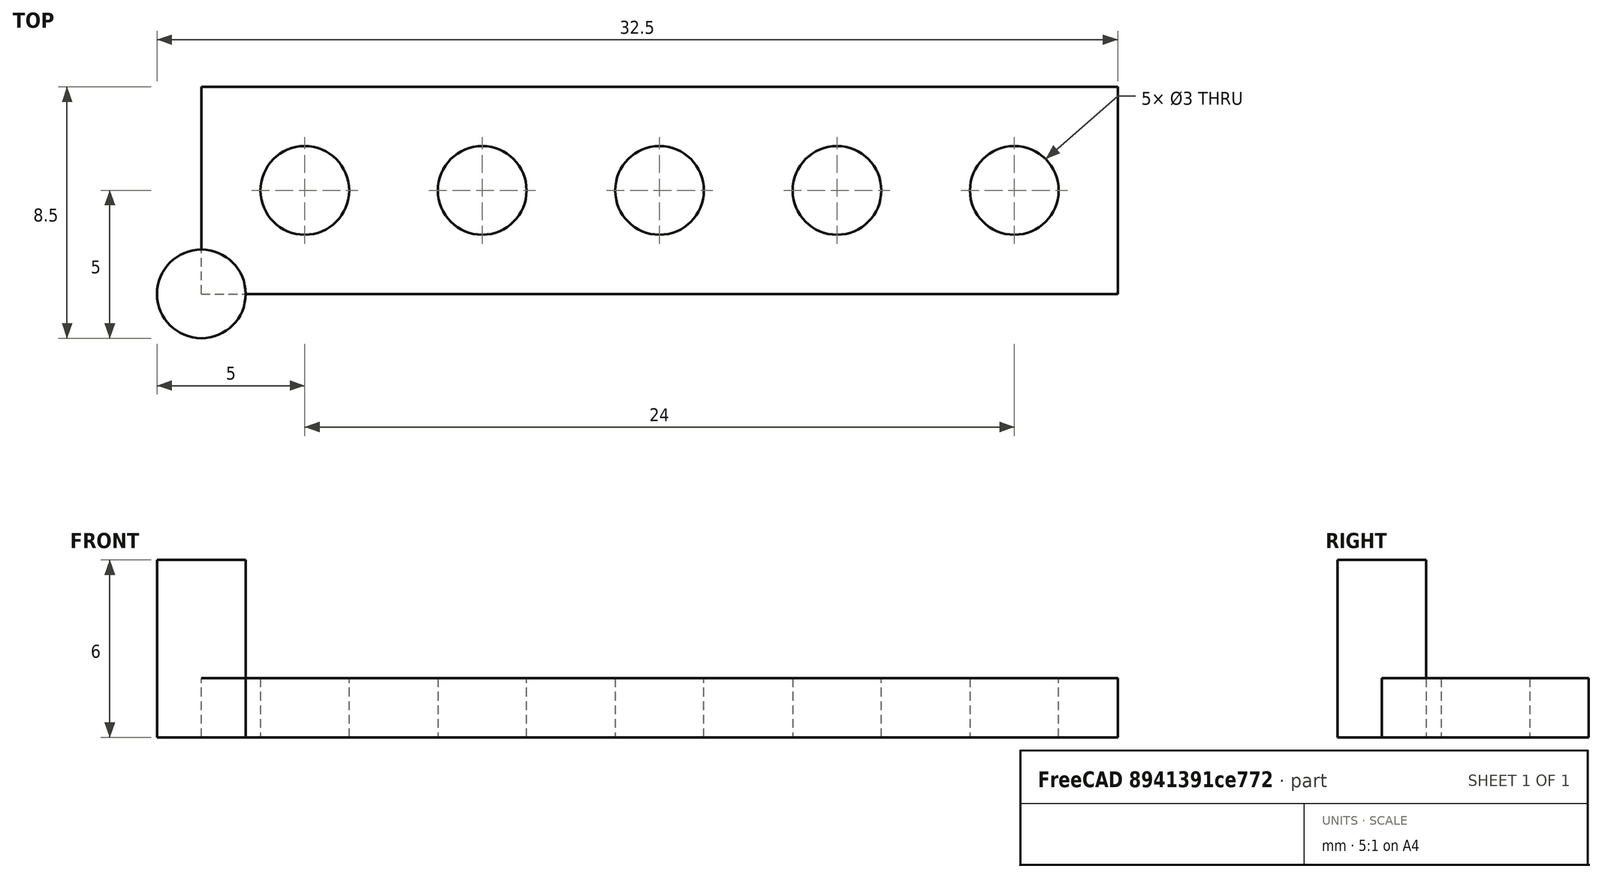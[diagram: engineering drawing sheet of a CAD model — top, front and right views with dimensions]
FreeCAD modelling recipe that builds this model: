
FCSTD DOCUMENT  (FreeCAD 0.21R33771 (Git))
Label: OJT1_T10R01_mecano
License: All rights reserved
LicenseURL: http://en.wikipedia.org/wiki/All_rights_reserved
objects: Part::Box×1, Part::Cylinder×1, Part::FeaturePython×1, Part::Cut×1
note: 3 computed .brp shape members not serialized (recipe doc carries the construction recipe); baked Part::Feature solids carry a one-line shape summary decoded from their .brp

FEATURE [Part::Box] Box  label="Cube"
  AttacherType = Attacher::AttachEngine3D
  Height = 2
  Length = 31
  Width = 7
FEATURE [Part::Cylinder] Cylinder
  Angle = 360
  AttacherType = Attacher::AttachEngine3D
  FirstAngle = 0
  Height = 6
  Radius = 1.5
  SecondAngle = 0
FEATURE [Part::FeaturePython] Array  # Draft array (typed FeaturePython)
  AlwaysSyncPlacement = false
  Angle = 360
  ArrayType = 0
  Axis = (0,0,1)
  Base = -> Cylinder
  Center = (0,0,0)
  Count = 5
  ExpandArray = false
  Fuse = false
  IntervalAxis = (0,0,0)
  IntervalX = (6,0,0)
  IntervalY = (0,0,0)
  IntervalZ = (0,0,0)
  NumberCircles = 3
  NumberPolar = 5
  NumberX = 5
  NumberY = 1
  NumberZ = 1
  Placement = pos=(3.5,3.5,-2) rot=(0,0,1;0rad)
  PlacementList = 5 placements: arithmetic series from (0,0,0) step (6,0,0) to (24,0,0)
  RadialDistance = 50
  ScaleList = (5) [(1,1,1),(1,1,1),(1,1,1),(1,1,1),(1,1,1)]
  Symmetry = 1
  TangentialDistance = 25
FEATURE [Part::Cut] Cut  label="peça_mecano"
  Base = -> Box
  Refine = true
  Tool = -> Array
